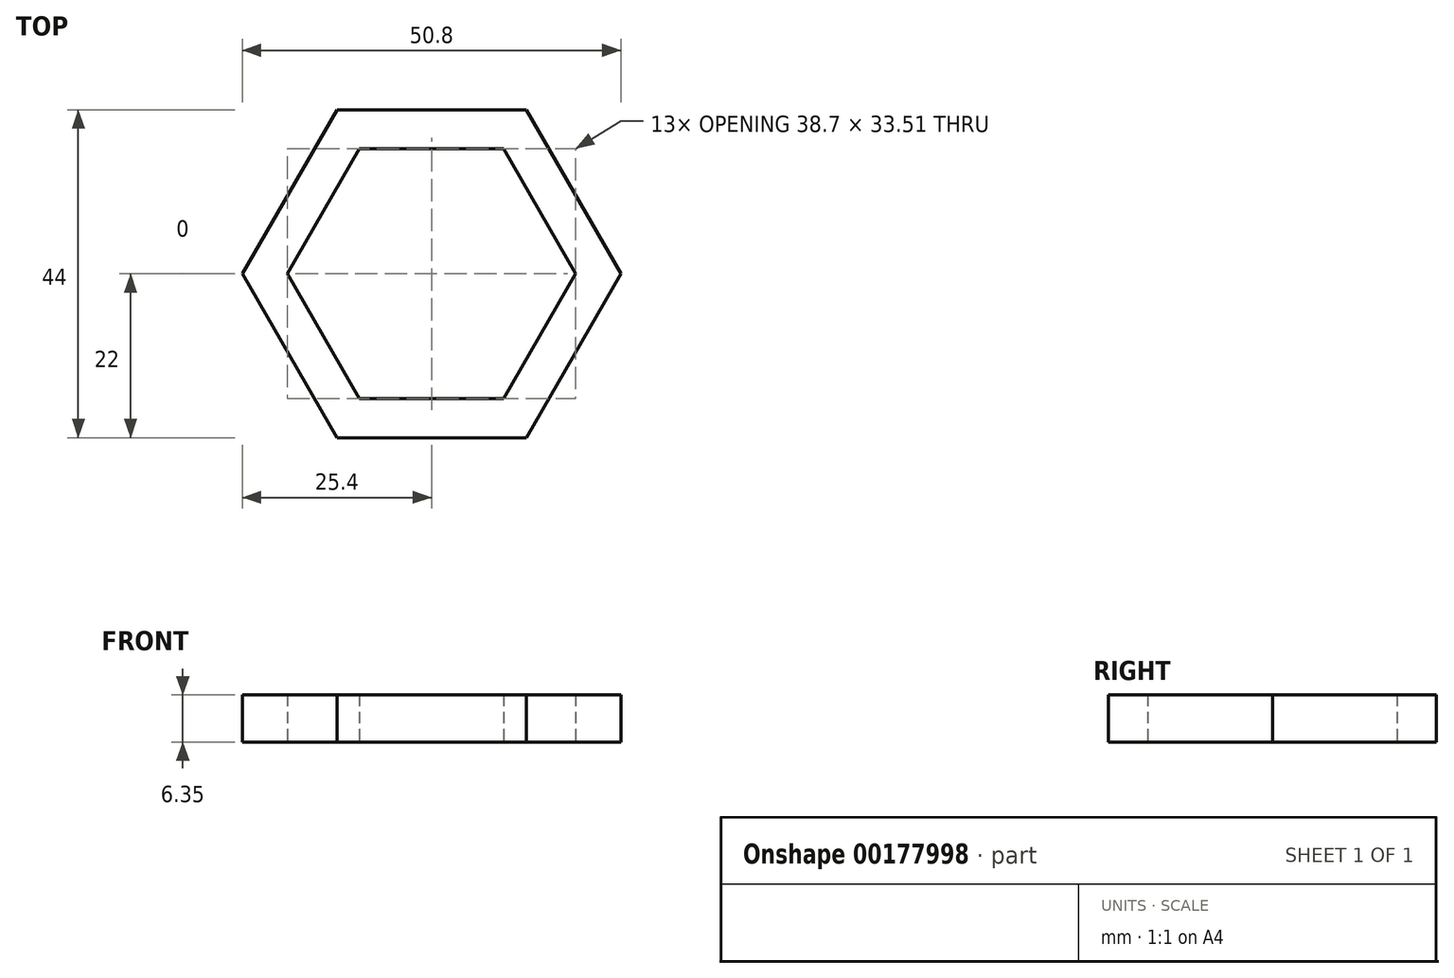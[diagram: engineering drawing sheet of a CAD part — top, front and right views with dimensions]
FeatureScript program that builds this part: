
annotation { "Feature Type Name" : "Feature", "Feature Type Description" : "" }
export const myFeature = defineFeature(function(context is Context, id is Id, definition is map)
    precondition{}
    {
        {
            var Q0;
            Q0=qCreatedBy(makeId("Top.planeOp"),FACE);
            var sketch = newSketch(context, id + "F0", { "sketchPlane" : qUnion([Q0])});
            skCircle(sketch, "E0.cCircle", {"center": v(0, 0) * mm, "radius": 22 * mm, "construction": true});
            skLineSegment(sketch, "E0.0", {"start": v(-12.7, 22) * mm, "end": v(12.7, 22) * mm});
            skLineSegment(sketch, "E0.1", {"start": v(12.7, 22) * mm, "end": v(25.4, 0) * mm});
            skLineSegment(sketch, "E0.2", {"start": v(25.4, 0) * mm, "end": v(12.7, -22) * mm});
            skLineSegment(sketch, "E0.3", {"start": v(12.7, -22) * mm, "end": v(-12.7, -22) * mm});
            skLineSegment(sketch, "E0.4", {"start": v(-12.7, -22) * mm, "end": v(-25.4, 0) * mm});
            skLineSegment(sketch, "E0.5", {"start": v(-25.4, 0) * mm, "end": v(-12.7, 22) * mm});
            skPoint(sketch, "E0.0.midPoint", {"position": v(0, 22) * mm});
            skCircle(sketch, "E1.cCircle", {"center": v(0, 44) * mm, "radius": 22 * mm, "construction": true});
            skLineSegment(sketch, "E1.0", {"start": v(12.7, 22) * mm, "end": v(-12.7, 22) * mm});
            skLineSegment(sketch, "E1.1", {"start": v(-12.7, 22) * mm, "end": v(-25.4, 44) * mm});
            skLineSegment(sketch, "E1.2", {"start": v(-25.4, 44) * mm, "end": v(-12.7, 66) * mm});
            skLineSegment(sketch, "E1.3", {"start": v(-12.7, 66) * mm, "end": v(12.7, 66) * mm});
            skLineSegment(sketch, "E1.4", {"start": v(12.7, 66) * mm, "end": v(25.4, 44) * mm});
            skLineSegment(sketch, "E1.5", {"start": v(25.4, 44) * mm, "end": v(12.7, 22) * mm});
            skCircle(sketch, "E2.cCircle", {"center": v(38.1, 22) * mm, "radius": 22 * mm, "construction": true});
            skLineSegment(sketch, "E2.0", {"start": v(12.7, 22) * mm, "end": v(25.4, 44) * mm});
            skLineSegment(sketch, "E2.1", {"start": v(25.4, 44) * mm, "end": v(50.8, 44) * mm});
            skLineSegment(sketch, "E2.2", {"start": v(50.8, 44) * mm, "end": v(63.5, 22) * mm});
            skLineSegment(sketch, "E2.3", {"start": v(63.5, 22) * mm, "end": v(50.8, 0) * mm});
            skLineSegment(sketch, "E2.4", {"start": v(50.8, 0) * mm, "end": v(25.4, 0) * mm});
            skLineSegment(sketch, "E2.5", {"start": v(25.4, 0) * mm, "end": v(12.7, 22) * mm});
            skPoint(sketch, "E2.0.midPoint", {"position": v(19.05, 33) * mm});
            skCircle(sketch, "E3.cCircle", {"center": v(0, 44) * mm, "radius": 17.16 * mm, "construction": true});
            skLineSegment(sketch, "E3.0", {"start": v(-9.9, 61.16) * mm, "end": v(9.9, 61.16) * mm});
            skLineSegment(sketch, "E3.1", {"start": v(9.9, 61.16) * mm, "end": v(19.82, 44) * mm});
            skLineSegment(sketch, "E3.2", {"start": v(19.82, 44) * mm, "end": v(9.9, 26.83) * mm});
            skLineSegment(sketch, "E3.3", {"start": v(9.9, 26.83) * mm, "end": v(-9.9, 26.83) * mm});
            skLineSegment(sketch, "E3.4", {"start": v(-9.9, 26.83) * mm, "end": v(-19.82, 44) * mm});
            skLineSegment(sketch, "E3.5", {"start": v(-19.82, 44) * mm, "end": v(-9.9, 61.16) * mm});
            skPoint(sketch, "E3.0.midPoint", {"position": v(0, 61.16) * mm});
            skCircle(sketch, "E4.cCircle", {"center": v(38.1, 22) * mm, "radius": 16.92 * mm, "construction": true});
            skLineSegment(sketch, "E4.0", {"start": v(28.33, 38.91) * mm, "end": v(47.87, 38.91) * mm});
            skLineSegment(sketch, "E4.1", {"start": v(47.87, 38.91) * mm, "end": v(57.63, 22) * mm});
            skLineSegment(sketch, "E4.2", {"start": v(57.63, 22) * mm, "end": v(47.87, 5.08) * mm});
            skLineSegment(sketch, "E4.3", {"start": v(47.87, 5.08) * mm, "end": v(28.33, 5.08) * mm});
            skLineSegment(sketch, "E4.4", {"start": v(28.33, 5.08) * mm, "end": v(18.57, 22) * mm});
            skLineSegment(sketch, "E4.5", {"start": v(18.57, 22) * mm, "end": v(28.33, 38.91) * mm});
            skPoint(sketch, "E4.0.midPoint", {"position": v(38.1, 38.91) * mm});
            skCircle(sketch, "E5.cCircle", {"center": v(0, 0) * mm, "radius": 16.76 * mm, "construction": true});
            skLineSegment(sketch, "E5.0", {"start": v(-9.67, 16.76) * mm, "end": v(9.67, 16.76) * mm});
            skLineSegment(sketch, "E5.1", {"start": v(9.67, 16.76) * mm, "end": v(19.35, 0) * mm});
            skLineSegment(sketch, "E5.2", {"start": v(19.35, 0) * mm, "end": v(9.67, -16.76) * mm});
            skLineSegment(sketch, "E5.3", {"start": v(9.67, -16.76) * mm, "end": v(-9.67, -16.76) * mm});
            skLineSegment(sketch, "E5.4", {"start": v(-9.67, -16.76) * mm, "end": v(-19.35, 0) * mm});
            skLineSegment(sketch, "E5.5", {"start": v(-19.35, 0) * mm, "end": v(-9.67, 16.76) * mm});
            skPoint(sketch, "E5.0.midPoint", {"position": v(0, 16.76) * mm});
            skSolve(sketch);
        }
        {
            var Q0;
            Q0=makeQuery(id+"F0.imprint","IMPRINT",FACE,{"disambiguationData":[TD([[makeQuery(id+"F0.imprint","IMPRINT",EDGE,{"derivedFrom":sQuery(id+"F0.wireOp",EDGE,"E1.0")}),-1.0]])]});
            var Q1;
            Q1=makeQuery(id+"F0.imprint","IMPRINT",FACE,{"disambiguationData":[TD([[makeQuery(id+"F0.imprint","IMPRINT",EDGE,{"derivedFrom":sQuery(id+"F0.wireOp",EDGE,"E2.0")}),-1.0]])]});
            var Q2;
            Q2=makeQuery(id+"F0.imprint","IMPRINT",FACE,{"disambiguationData":[TD([[makeQuery(id+"F0.imprint","IMPRINT",EDGE,{"derivedFrom":sQuery(id+"F0.wireOp",EDGE,"E0.2")}),-1.0]])]});
            extrude(context, id + "F1", {"entities" : qUnion([Q0, Q1, Q2]), "depth" : 6.35 * mm});
        }
    });
